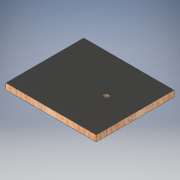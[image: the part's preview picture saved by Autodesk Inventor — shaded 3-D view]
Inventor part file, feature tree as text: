
AUTODESK INVENTOR PART (.ipt)
format: ipt  version: 2017 (Build 210142000, 142)  size: 130,048 bytes
history: native  units: in
note: dims shown in document units (in); Inventor stores cm internally (conversion verified against a paired STEP export)
features: extrude x2, sketch x2, projected_geometry x1
ambient origin geometry x8: Origin, YZ Plane, XZ Plane, XY Plane, X Axis, Y Axis, Z Axis, Center Point
bodies: Solid1 (feature_tree)
feature tree (5):
  extrude  "Extrusion1"  Depth=6.0in
  extrude  "Extrusion2"  Depth=0.4688in
  sketch  "Sketch1"  dims[d0=6.9688in d1=6.0in]
  sketch  "Sketch2"  dims[d2=0.4688in d3=0.0in d4=2.2188in d5=0.375in d6=0.4688in d7=0.0in]
  projected_geometry  "Projected Loop1"
